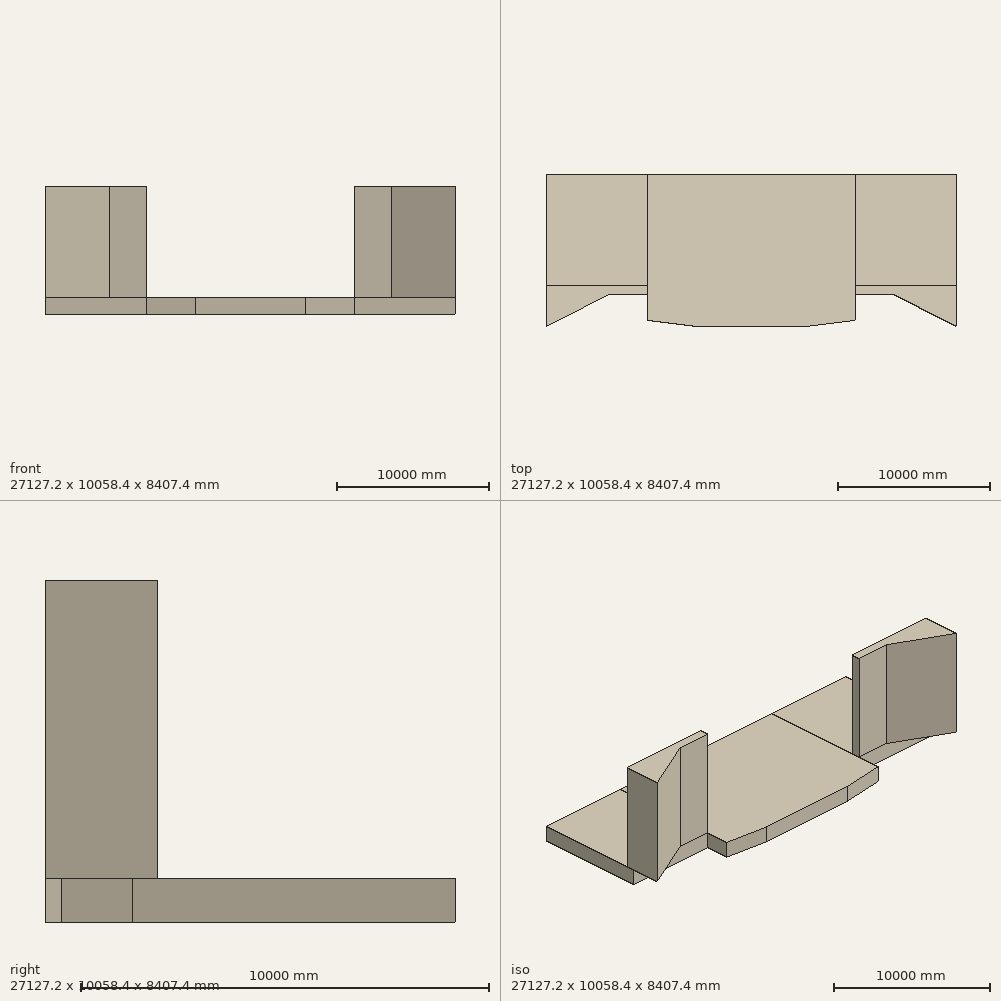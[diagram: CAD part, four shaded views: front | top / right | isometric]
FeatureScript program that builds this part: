
annotation { "Feature Type Name" : "Feature", "Feature Type Description" : "" }
export const myFeature = defineFeature(function(context is Context, id is Id, definition is map)
    precondition{}
    {
        {
            var Q0;
            Q0=qCreatedBy(makeId("Top.planeOp"),FACE);
            var sketch = newSketch(context, id + "F0", { "sketchPlane" : qUnion([Q0])});
            skLineSegment(sketch, "E0.top", {"start": v(-3550.45, 11071.74) * mm, "end": v(10165.55, 11071.74) * mm});
            skLineSegment(sketch, "E0.left", {"start": v(-3550.45, 1413.4) * mm, "end": v(-3550.45, 11071.74) * mm});
            skLineSegment(sketch, "E0.right", {"start": v(10165.55, 1413.4) * mm, "end": v(10165.55, 11071.74) * mm});
            skLineSegment(sketch, "E1", {"start": v(3307.55, 1013.34) * mm, "end": v(6965.15, 1013.34) * mm});
            skLineSegment(sketch, "E2", {"start": v(6965.15, 1013.34) * mm, "end": v(10165.55, 1413.4) * mm});
            skLineSegment(sketch, "E3.MirrorCS", {"start": v(6965.15, 21130.14) * mm, "end": v(10165.55, 20730.1) * mm});
            skLineSegment(sketch, "E4.MirrorCS", {"start": v(3307.55, 21130.14) * mm, "end": v(6965.15, 21130.14) * mm});
            skLineSegment(sketch, "E5.MirrorCS", {"start": v(3307.55, 1013.34) * mm, "end": v(-350.05, 1013.34) * mm});
            skLineSegment(sketch, "E6.MirrorCS", {"start": v(-350.05, 1013.34) * mm, "end": v(-3550.45, 1413.4) * mm});
            skPoint(sketch, "E7.end.orphan", {"position": v(3307.55, 11071.74) * mm});
            skSolve(sketch);
        }
        {
            var Q0;
            Q0=qSketchRegion(id+"F0",true);
            extrude(context, id + "F1", {"entities" : qUnion([Q0]), "depth" : -1092.2 * mm});
        }
        {
            var Q0;
            Q0=makeQuery(id+"F1.opExtrude","CAP_FACE",FACE,{"disambiguationData":[OSD([sQuery(id+"F0.wireOp",EDGE,"E0.top"),sQuery(id+"F0.wireOp",EDGE,"E0.left"),sQuery(id+"F0.wireOp",EDGE,"E0.right"),sQuery(id+"F0.wireOp",EDGE,"E1"),sQuery(id+"F0.wireOp",EDGE,"E2"),sQuery(id+"F0.wireOp",EDGE,"E5.MirrorCS"),sQuery(id+"F0.wireOp",EDGE,"E6.MirrorCS")])],"isStart":true});
            var sketch = newSketch(context, id + "F2", { "sketchPlane" : qUnion([Q0])});
            skLineSegment(sketch, "E8", {"start": v(10165.55, 3756.54) * mm, "end": v(10165.55, 3146.94) * mm});
            skLineSegment(sketch, "E9", {"start": v(10165.55, 3146.94) * mm, "end": v(12662.12, 3146.94) * mm});
            skLineSegment(sketch, "E10", {"start": v(12662.12, 3146.94) * mm, "end": v(16871.15, 1013.34) * mm});
            skLineSegment(sketch, "E11", {"start": v(16871.15, 1013.34) * mm, "end": v(16871.15, 3756.54) * mm});
            skLineSegment(sketch, "E12", {"start": v(16871.15, 3756.54) * mm, "end": v(10165.55, 3756.54) * mm});
            skLineSegment(sketch, "E13.MirrorCS", {"start": v(-10256.05, 3756.54) * mm, "end": v(-3550.45, 3756.54) * mm});
            skLineSegment(sketch, "E14.MirrorCS", {"start": v(-10256.05, 1013.34) * mm, "end": v(-10256.05, 3756.54) * mm});
            skLineSegment(sketch, "E15.MirrorCS", {"start": v(-3550.45, 3146.94) * mm, "end": v(-6047.02, 3146.94) * mm});
            skLineSegment(sketch, "E16.MirrorCS", {"start": v(-3550.45, 3756.54) * mm, "end": v(-3550.45, 3146.94) * mm});
            skLineSegment(sketch, "E17.MirrorCS", {"start": v(-6047.02, 3146.94) * mm, "end": v(-10256.05, 1013.34) * mm});
            skSolve(sketch);
        }
        {
            var Q0;
            Q0=qSketchRegion(id+"F2",true);
            extrude(context, id + "F3", {"entities" : qUnion([Q0]), "depth" : 7315.2 * mm});
        }
        {
            var Q0;
            Q0=makeQuery(id+"F1.opExtrude","SWEPT_FACE",FACE,{"disambiguationData":[OSD([sQuery(id+"F0.wireOp",EDGE,"E0.left")])]});
            var sketch = newSketch(context, id + "F4", { "sketchPlane" : qUnion([Q0])});
            skLineSegment(sketch, "E18.bottom", {"start": v(-11071.74, -1092.2) * mm, "end": v(-3146.94, -1092.2) * mm});
            skLineSegment(sketch, "E18.top", {"start": v(-11071.74, 0) * mm, "end": v(-3146.94, 0) * mm});
            skLineSegment(sketch, "E18.left", {"start": v(-11071.74, -1092.2) * mm, "end": v(-11071.74, 0) * mm});
            skLineSegment(sketch, "E18.right", {"start": v(-3146.94, -1092.2) * mm, "end": v(-3146.94, 0) * mm});
            skSolve(sketch);
        }
        {
            var Q0;
            Q0=qSketchRegion(id+"F4",true);
            extrude(context, id + "F5", {"entities" : qUnion([Q0]), "depth" : 6705.6 * mm});
        }
        {
            var Q0;
            Q0=makeQuery(id+"F1.opExtrude","SWEPT_FACE",FACE,{"disambiguationData":[OSD([sQuery(id+"F0.wireOp",EDGE,"E0.right")])]});
            var sketch = newSketch(context, id + "F6", { "sketchPlane" : qUnion([Q0])});
            skLineSegment(sketch, "E19.bottom", {"start": v(11071.74, -1092.2) * mm, "end": v(3146.94, -1092.2) * mm});
            skLineSegment(sketch, "E19.top", {"start": v(11071.74, 0) * mm, "end": v(3146.94, 0) * mm});
            skLineSegment(sketch, "E19.left", {"start": v(11071.74, -1092.2) * mm, "end": v(11071.74, 0) * mm});
            skLineSegment(sketch, "E19.right", {"start": v(3146.94, -1092.2) * mm, "end": v(3146.94, 0) * mm});
            skSolve(sketch);
        }
        {
            var Q0;
            Q0=qSketchRegion(id+"F6",true);
            extrude(context, id + "F7", {"entities" : qUnion([Q0]), "depth" : 6705.6 * mm});
        }
        {
            var Q0;
            Q0=makeQuery(id+"F1.opExtrude","SWEPT_FACE",FACE,{"disambiguationData":[OSD([sQuery(id+"F0.wireOp",EDGE,"E1"),sQuery(id+"F0.wireOp",EDGE,"E5.MirrorCS")])]});
            var sketch = newSketch(context, id + "F8", { "sketchPlane" : qUnion([Q0])});
            skLineSegment(sketch, "E20.bottom", {"start": v(2108.43, -2604.6) * mm, "end": v(2489.43, -2604.6) * mm});
            skLineSegment(sketch, "E20.top", {"start": v(2108.43, -2858.6) * mm, "end": v(2489.43, -2858.6) * mm});
            skLineSegment(sketch, "E20.left", {"start": v(2108.43, -2604.6) * mm, "end": v(2108.43, -2858.6) * mm});
            skLineSegment(sketch, "E20.right", {"start": v(2489.43, -2604.6) * mm, "end": v(2489.43, -2858.6) * mm});
            skSolve(sketch);
        }
        {
            var Q0;
            Q0=qSketchRegion(id+"F8",true);
            extrude(context, id + "F9", {"entities" : qUnion([Q0]), "depth" : 1066.8 * mm});
        }
        {
            var Q0;
            Q0=makeQuery(id+"F9.opExtrude","SWEPT_FACE",FACE,{"disambiguationData":[OSD([sQuery(id+"F8.wireOp",EDGE,"E20.bottom")])]});
            shell(context, id + "F10", {"entities" : qUnion([Q0]), "thickness" : 19.05 * mm});
        }
        {
            var Q0;
            Q0=makeQuery(id+"F9.opExtrude","SWEPT_BODY",BODY,{"disambiguationData":[OSD([sQuery(id+"F8.wireOp",EDGE,"E20.bottom"),sQuery(id+"F8.wireOp",EDGE,"E20.top"),sQuery(id+"F8.wireOp",EDGE,"E20.left"),sQuery(id+"F8.wireOp",EDGE,"E20.right")])]});
            deleteBodies(context, id + "F11", {"entities" : qUnion([Q0])});
        }
    });
